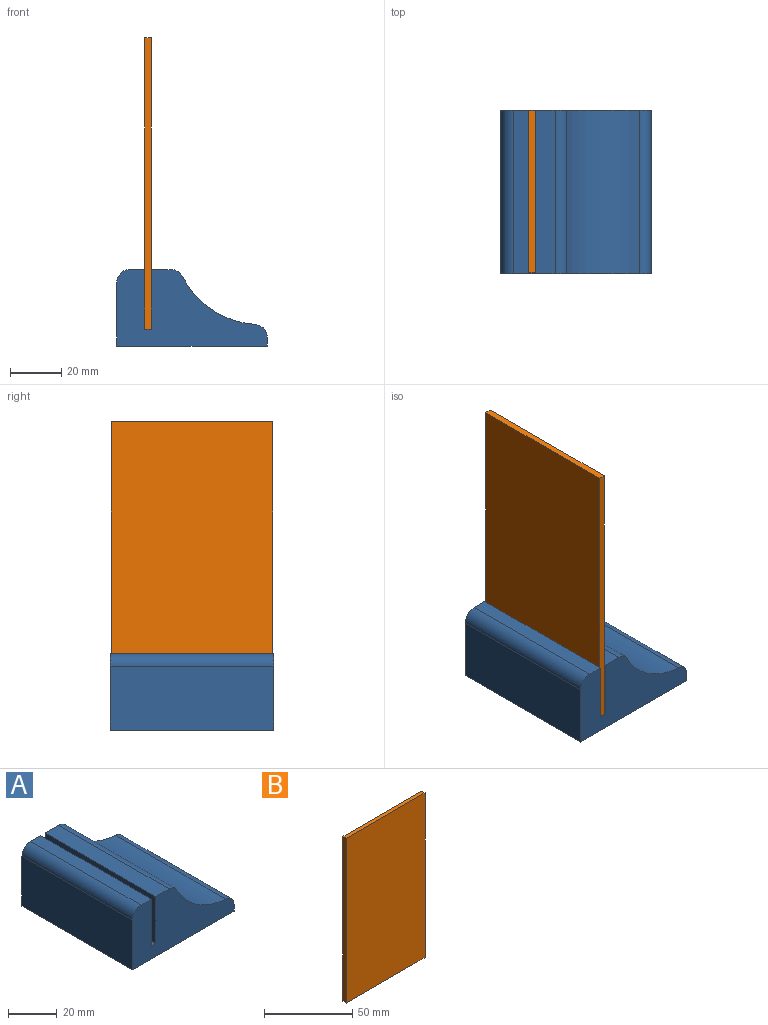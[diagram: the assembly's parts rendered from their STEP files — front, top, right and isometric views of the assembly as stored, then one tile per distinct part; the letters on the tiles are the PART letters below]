
ASSEMBLY  parts=2 mates=1
PART A: 14 faces, bbox 58.9x64x30 mm
  f0: plane 64x7.72mm, normal (0,0,1), area 494.1mm2, adj f1,f7,f8,f11
  f1: plane 58.88x30mm, normal (0,-1,0), area 1141.2mm2, adj f0,f2,f3,f4,f5,f6,f8,f9
  f2: cylinder r=34.62mm len=64mm, axis (0,1,0), area 2285.6mm2, adj f1,f7,f11,f13
  f3: plane 64x5.93mm, normal (0,0,1), area 379.3mm2, adj f1,f7,f9,f12
  f4: plane 64x25mm, normal (-1,0,0), area 1600mm2, adj f1,f5,f7,f12
  f5: plane 64x58.88mm, normal (0,0,-1), area 3768mm2, adj f1,f4,f6,f7
  f6: plane 64x3.49mm, normal (1,0,0), area 223.1mm2, adj f1,f5,f7,f13
  f7: plane 58.88x30mm, normal (0,1,0), area 1141.2mm2, adj f0,f2,f3,f4,f5,f6,f8,f9
  f8: plane 64x23.4mm, normal (-1,0,0), area 1497.6mm2, adj f0,f1,f7,f10
  f9: plane 64x23.4mm, normal (1,0,0), area 1497.6mm2, adj f1,f3,f7,f10
  f10: plane 64x2.6mm, normal (0,0,1), area 166.4mm2, adj f1,f7,f8,f9
  f11: cylinder r=5mm len=64mm, axis (0,1,0), area 351.6mm2, adj f0,f1,f2,f7
  f12: cylinder r=5mm len=64mm, axis (0,-1,0), area 502.7mm2, adj f1,f3,f4,f7
  f13: cylinder r=5mm len=64mm, axis (0,1,0), area 481.2mm2, adj f1,f2,f6,f7
PART B: 6 faces, bbox 63.1x2.5x114.1 mm
  f0: plane 114.11x2.52mm, normal (1,0,0), area 287.6mm2, adj f1,f3,f4,f5
  f1: plane 63.13x2.52mm, normal (0,0,1), area 159.1mm2, adj f0,f2,f4,f5
  f2: plane 114.11x2.52mm, normal (-1,0,0), area 287.6mm2, adj f1,f3,f4,f5
  f3: plane 63.13x2.52mm, normal (0,0,-1), area 159.1mm2, adj f0,f2,f4,f5
  f4: plane 114.11x63.13mm, normal (0,-1,0), area 7203.8mm2, adj f0,f1,f2,f3
  f5: plane 114.11x63.13mm, normal (0,1,0), area 7203.8mm2, adj f0,f1,f2,f3
PLACE A at identity
PLACE B rot(axis=(0,0,1),90deg) t=(10.97,-31.48,15.29)mm
MATE fastened B.f3 <-> A.f10  axis (0,0,-1) through (12.23,-32,-28.6)mm
